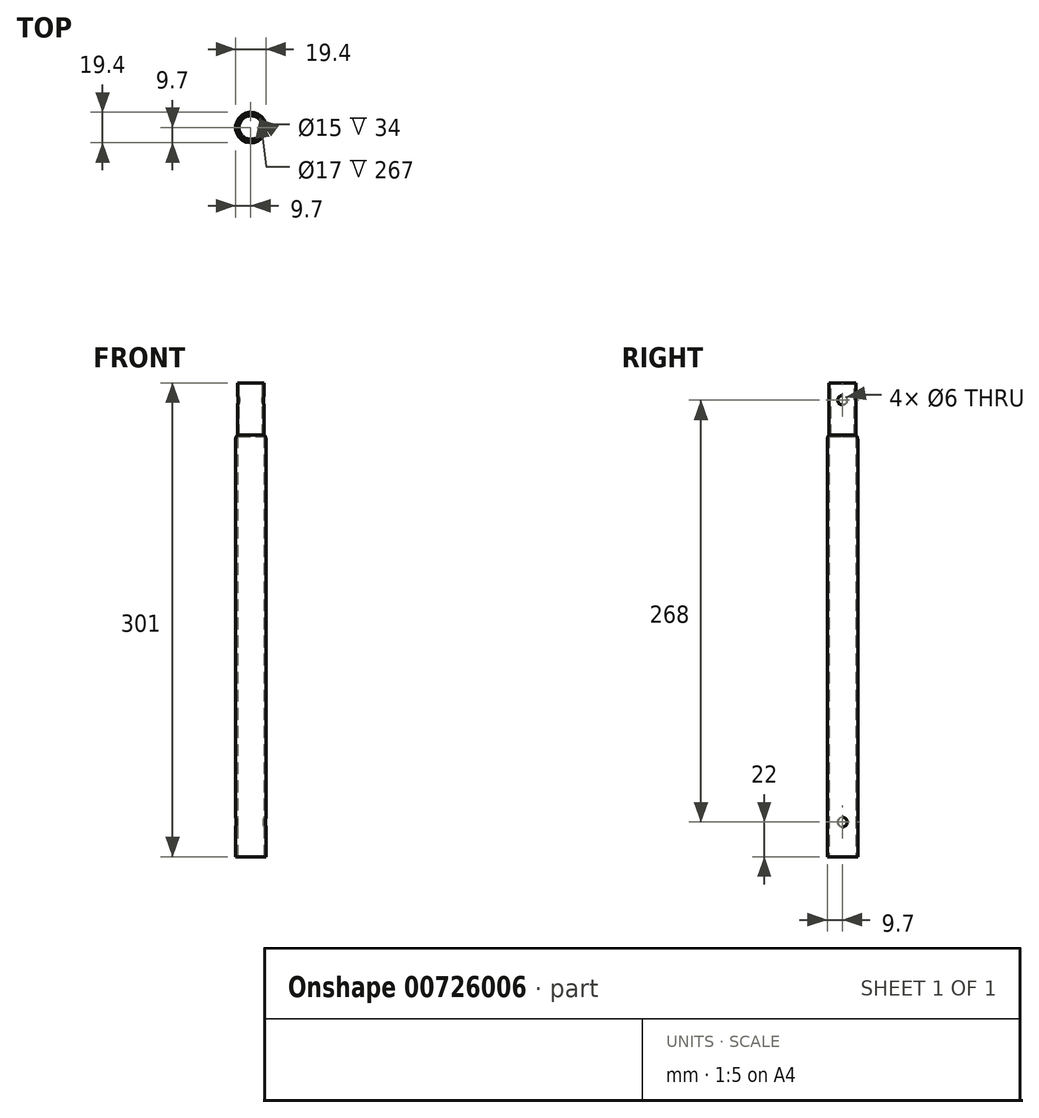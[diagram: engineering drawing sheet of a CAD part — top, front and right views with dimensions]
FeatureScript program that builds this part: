
annotation { "Feature Type Name" : "Feature", "Feature Type Description" : "" }
export const myFeature = defineFeature(function(context is Context, id is Id, definition is map)
    precondition{}
    {
        {
            var Q0;
            Q0=qCreatedBy(makeId("Top.planeOp"),FACE);
            var sketch = newSketch(context, id + "F0", { "sketchPlane" : qUnion([Q0])});
            skCircle(sketch, "E0", {"center": v(0, 0) * mm, "radius": 9.7 * mm});
            skSolve(sketch);
        }
        {
            var Q0;
            Q0=makeQuery(id+"F0.imprint","IMPRINT",FACE,{"disambiguationData":[TD([[makeQuery(id+"F0.imprint","IMPRINT",EDGE,{"derivedFrom":sQuery(id+"F0.wireOp",EDGE,"E0")}),1.0]])]});
            extrude(context, id + "F1", {"entities" : qUnion([Q0]), "depth" : 268 * mm, "offsetDistance" : 25 * mm});
        }
        {
            var Q0;
            Q0=makeQuery(id+"F1.opExtrude","CAP_FACE",FACE,{"disambiguationData":[OSD([sQuery(id+"F0.wireOp",EDGE,"E0")])],"isStart":false});
            var sketch = newSketch(context, id + "F2", { "sketchPlane" : qUnion([Q0])});
            skCircle(sketch, "E1", {"center": v(0, 0) * mm, "radius": 8.5 * mm});
            skSolve(sketch);
        }
        {
            var Q0;
            Q0=makeQuery(id+"F2.imprint","IMPRINT",FACE,{"disambiguationData":[TD([[makeQuery(id+"F2.imprint","IMPRINT",EDGE,{"derivedFrom":sQuery(id+"F2.wireOp",EDGE,"E1")}),1.0]])]});
            extrude(context, id + "F3", {"entities" : qUnion([Q0]), "operationType" : NewBodyOperationType.ADD, "depth" : 33 * mm, "offsetDistance" : 25 * mm});
        }
        {
            var Q0;
            Q0=qCreatedBy(makeId("Right.planeOp"),FACE);
            var sketch = newSketch(context, id + "F4", { "sketchPlane" : qUnion([Q0])});
            skPoint(sketch, "E2", {"position": v(0, 22) * mm});
            skCircle(sketch, "E3", {"center": v(0, 22) * mm, "radius": 3 * mm});
            skPoint(sketch, "E4", {"position": v(0, 0) * mm});
            skPoint(sketch, "E5", {"position": v(0, 290) * mm});
            skCircle(sketch, "E6", {"center": v(0, 290) * mm, "radius": 3 * mm});
            skSolve(sketch);
        }
        {
            var Q0;
            Q0=makeQuery(id+"F3.opExtrude","CAP_FACE",FACE,{"disambiguationData":[OSD([sQuery(id+"F2.wireOp",EDGE,"E1")])],"isStart":false});
            var sketch = newSketch(context, id + "F5", { "sketchPlane" : qUnion([Q0])});
            skCircle(sketch, "E7", {"center": v(0, 0) * mm, "radius": 7.5 * mm});
            skSolve(sketch);
        }
        {
            var Q0;
            Q0=makeQuery(id+"F5.imprint","IMPRINT",FACE,{"disambiguationData":[TD([[makeQuery(id+"F5.imprint","IMPRINT",EDGE,{"derivedFrom":sQuery(id+"F5.wireOp",EDGE,"E7")}),1.0]])]});
            extrude(context, id + "F6", {"entities" : qUnion([Q0]), "operationType" : NewBodyOperationType.REMOVE, "oppositeDirection" : true, "depth" : 36.4 * mm, "offsetDistance" : 25 * mm});
        }
        {
            var Q0;
            Q0=makeQuery(id+"F1.opExtrude","CAP_FACE",FACE,{"disambiguationData":[OSD([sQuery(id+"F0.wireOp",EDGE,"E0")])],"isStart":true});
            var sketch = newSketch(context, id + "F7", { "sketchPlane" : qUnion([Q0])});
            skCircle(sketch, "E8", {"center": v(0, 0) * mm, "radius": 8.5 * mm});
            skSolve(sketch);
        }
        {
            var Q0;
            Q0 = qSketchRegion(id + "F7", true);
            extrude(context, id + "F8", {"entities" : qUnion([Q0]), "operationType" : NewBodyOperationType.REMOVE, "oppositeDirection" : true, "depth" : 267 * mm, "offsetDistance" : 25 * mm});
        }
        {
            var Q0;
            Q0 = qSketchRegion(id + "F4", true);
            extrude(context, id + "F9", {"entities" : qUnion([Q0]), "operationType" : NewBodyOperationType.REMOVE, "oppositeDirection" : true, "depth" : 25 * mm, "offsetDistance" : 25 * mm, "hasSecondDirection" : true, "secondDirectionOppositeDirection" : false, "secondDirectionDepth" : 25 * mm});
        }
        {
            var Q0;
            Q0=makeQuery(id+"F1.opExtrude","CAP_EDGE",EDGE,{"disambiguationData":[OSD([sQuery(id+"F0.wireOp",EDGE,"E0")])],"isStart":false});
            fillet(context, id + "F10", {"entities" : qUnion([Q0]), "radius" : 5 * mm, "rho" : 0.5, "crossSection" : FilletCrossSection.CONIC, "allowEdgeOverflow" : false});
        }
    });
